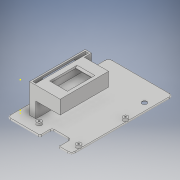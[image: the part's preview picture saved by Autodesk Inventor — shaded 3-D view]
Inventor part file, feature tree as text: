
AUTODESK INVENTOR PART (.ipt)
format: ipt  version: 2019 (Build 230136000, 136)  size: 548,352 bytes
history: native  units: in
note: dims shown in document units (in); Inventor stores cm internally (conversion verified against a paired STEP export)
features: sketch x21, extrude x13, hole x4, chamfer x3, fillet x2
ambient origin geometry x8: Origin, YZ Plane, XZ Plane, XY Plane, X Axis, Y Axis, Z Axis, Center Point
bodies: Solid1 (feature_tree)
feature tree (43):
  extrude  "Extrusion1"  Depth=0.0787in
  sketch  "Sketch2"  dims[d6=0.0591in d7=0.2362in]
  extrude  "Extrusion2"  Depth=0.2362in
  hole  "Hole1"  [1 undecoded]
  hole  "Hole2"  [1 undecoded]
  sketch  "Sketch6"  dims[d14=0.1181in d15=0.0in]
  sketch  "Sketch7"  dims[d16=0.0793in d17=0.1181in d18=0.1575in d19=0.0787in d20=90.0deg d21=0.2992in d22=0.8108in]
  sketch  "Sketch8"  dims[d23=0.0793in d24=0.1181in d25=0.1575in d26=0.0787in d27=90.0deg d28=0.2992in d29=0.8108in]
  hole  "Hole3"  [1 undecoded]
  extrude  "Extrusion3"  Depth=0.0787in
  hole  "Hole4"  [1 undecoded]
  sketch  "Sketch9"  dims[d30=0.0793in d31=0.1181in d32=0.1575in d33=0.0787in d34=90.0deg d35=0.2992in d36=0.8108in]
  extrude  "Extrusion4"  Depth=1.1811in
  extrude  "Extrusion5"  Depth=0.6693in TaperAngle=0.0deg
  extrude  "Extrusion6"  Depth=0.0787in
  extrude  "Extrusion7"  Depth=0.4724in
  fillet  "Fillet1"  Radius=2.2441in
  extrude  "Extrusion10"  Depth=0.1575in
  chamfer  "Chamfer1"  Distance=0.0984in
  sketch  "Sketch19"  dims[d55=1.1024in d56=0.4724in d57=2.2441in d58=0.0in]
  extrude  "Extrusion12"  Depth=0.8661in
  chamfer  "Chamfer2"  Distance=0.6693in
  sketch  "Sketch22"  dims[d61=0.8661in]
  extrude  "Extrusion13"  Depth=0.0394in TaperAngle=0.0deg
  extrude  "Extrusion14"  Depth=0.0787in TaperAngle=45.0deg
  extrude  "Extrusion15"  Depth=0.0394in
  extrude  "Extrusion16"  Depth=0.0394in
  chamfer  "Chamfer4"  Distance=0.2362in
  fillet  "Fillet3"  Radius=0.3937in
  sketch  "Sketch1"  dims[d0=3.1811in d1=4.9921in d2=0.1969in d3=0.0787in d4=0.0in d5=0.4921in]
  sketch  "Sketch3"  dims[d8=1.9291in d9=2.2835in]
  sketch  "Sketch4"  dims[d10=1.9291in d11=0.2362in]
  sketch  "Sketch5"  dims[d12=0.2362in d13=0.2362in]
  sketch  "Sketch10"  dims[d37=0.0793in d38=0.1181in d39=0.1575in d40=0.0787in d41=90.0deg d42=0.2992in d43=0.8108in d44=2.3622in]
  sketch  "Sketch11"  dims[d45=0.1575in d46=2.9921in]
  sketch  "Sketch12"  dims[d47=1.4173in d48=0.0in d49=1.1811in]
  sketch  "Sketch13"  dims[d50=2.3622in d51=0.6693in d52=0.0in]
  sketch  "Sketch14"  dims[d53=0.0984in d54=0.0787in]
  sketch  "Sketch21"  dims[d59=0.5906in d60=0.1575in]
  sketch  "Sketch23"  dims[d62=1.1811in d63=0.0984in d64=0.0in]
  sketch  "Sketch24"  dims[d65=0.6693in d66=0.8661in]
  sketch  "Sketch25"  dims[d67=0.5906in d68=0.6693in d69=0.0in]
  sketch  "Sketch26"  dims[d70=0.0787in d77=0.5118in d78=0.0in d83=0.0787in d84=0.0787in d85=45.0deg d88=1.1811in d89=0.2559in d90=0.2362in d91=0.3937in d92=0.0in d93=0.0787in d94=0.0787in d95=45.0deg d96=0.1575in d97=2.7165in d98=0.3937in d99=0.0in d100=0.3937in d101=0.0in d102=0.0787in d103=0.0787in d104=0.0787in d105=0.0787in d106=1.1417in d107=0.0in d108=0.1575in d109=0.5906in d110=1.5748in d111=0.3937in d112=0.3937in d113=0.0in d117=0.0787in d118=0.0787in d119=45.0deg d120=0.0394in]
note: 4 required parameter values undecoded (feature->parameter linkage not recoverable at this tier; creation-order binding heuristic only, values carry confidence <= 0.55)
